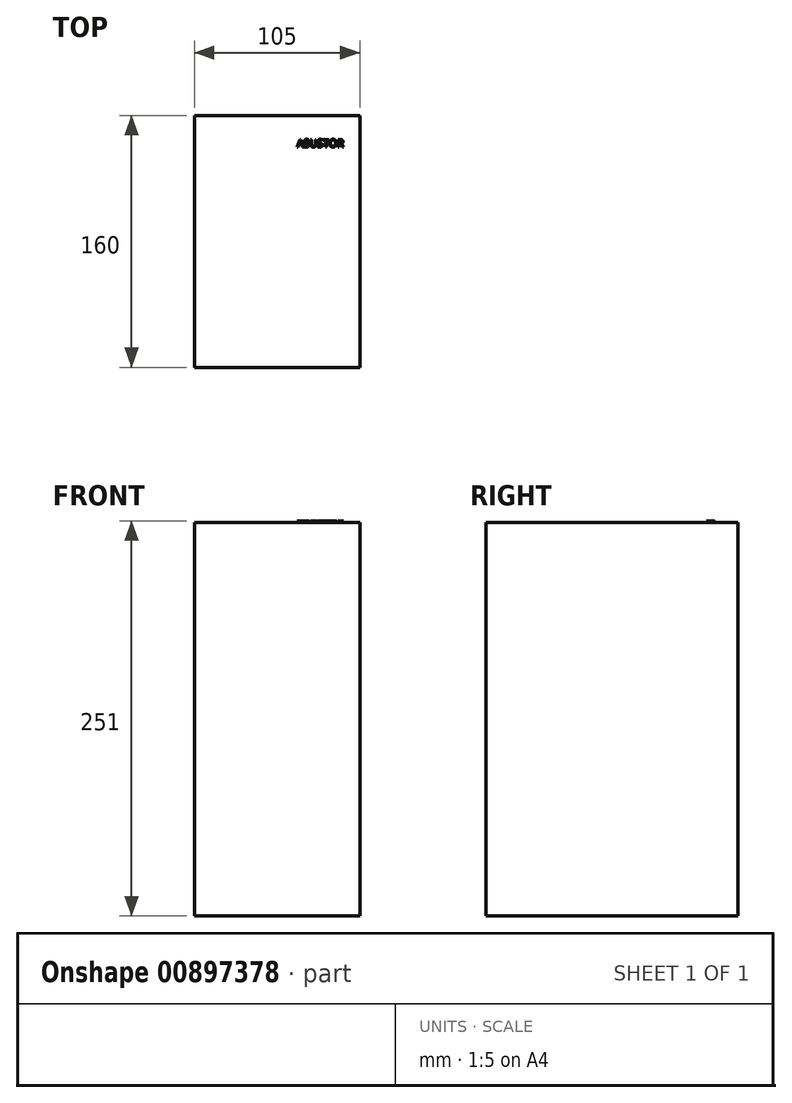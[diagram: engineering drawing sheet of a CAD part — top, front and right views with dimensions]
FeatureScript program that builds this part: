
annotation { "Feature Type Name" : "Feature", "Feature Type Description" : "" }
export const myFeature = defineFeature(function(context is Context, id is Id, definition is map)
    precondition{}
    {
        {
            var Q0;
            Q0=qCreatedBy(makeId("Top.planeOp"),FACE);
            var sketch = newSketch(context, id + "F0", { "sketchPlane" : qUnion([Q0])});
            skLineSegment(sketch, "E0.bottom", {"start": v(0, 0) * mm, "end": v(-105, 0) * mm});
            skLineSegment(sketch, "E0.top", {"start": v(0, 160) * mm, "end": v(-105, 160) * mm});
            skLineSegment(sketch, "E0.left", {"start": v(0, 0) * mm, "end": v(0, 160) * mm});
            skLineSegment(sketch, "E0.right", {"start": v(-105, 0) * mm, "end": v(-105, 160) * mm});
            skSolve(sketch);
        }
        {
            var Q0;
            Q0 = qSketchRegion(id + "F0", true);
            extrude(context, id + "F1", {"entities" : qUnion([Q0]), "depth" : 250 * mm, "offsetDistance" : 25 * mm});
        }
        {
            var Q0;
            Q0=makeQuery(id+"F1.opExtrude","CAP_FACE",FACE,{"disambiguationData":[OSD([sQuery(id+"F0.wireOp",EDGE,"E0.bottom"),sQuery(id+"F0.wireOp",EDGE,"E0.top"),sQuery(id+"F0.wireOp",EDGE,"E0.left"),sQuery(id+"F0.wireOp",EDGE,"E0.right")])],"isStart":false});
            var sketch = newSketch(context, id + "F2", { "sketchPlane" : qUnion([Q0])});
            skText(sketch, "E1", { "text": "ASUSTOR", "fontName": "OpenSans-Regular.ttf"});
            const initialGuessF2  = {"E1": [-0.04, 0.14, 1, 0, 0.00485]};
            skSetInitialGuess(sketch, initialGuessF2);
            skSolve(sketch);
        }
        {
            var Q0;
            Q0 = qSketchRegion(id + "F2", true);
            extrude(context, id + "F3", {"entities" : qUnion([Q0]), "operationType" : NewBodyOperationType.ADD, "depth" : 1 * mm, "offsetDistance" : 25 * mm});
        }
    });
